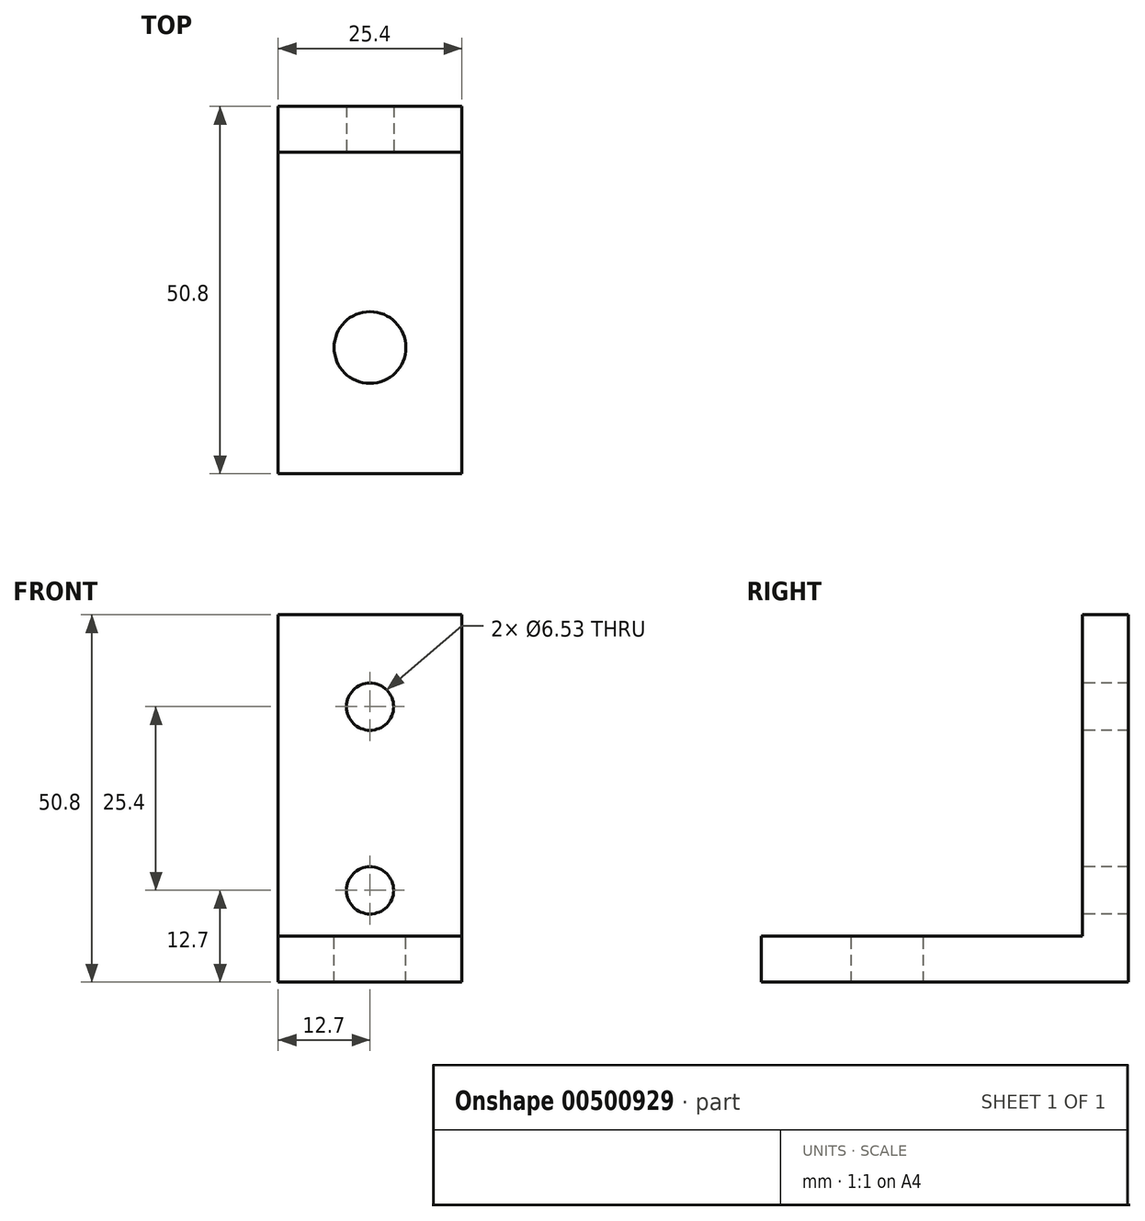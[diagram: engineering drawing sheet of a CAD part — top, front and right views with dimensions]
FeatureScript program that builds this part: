
annotation { "Feature Type Name" : "Feature", "Feature Type Description" : "" }
export const myFeature = defineFeature(function(context is Context, id is Id, definition is map)
    precondition{}
    {
        {
            var Q0;
            Q0=qCreatedBy(makeId("Right.planeOp"),FACE);
            var sketch = newSketch(context, id + "F0", { "sketchPlane" : qUnion([Q0])});
            skLineSegment(sketch, "E0.bottom", {"start": v(0, 0) * mm, "end": v(-50.8, 0) * mm});
            skLineSegment(sketch, "E0.top", {"start": v(0, 6.35) * mm, "end": v(-50.8, 6.35) * mm});
            skLineSegment(sketch, "E0.left", {"start": v(0, 0) * mm, "end": v(0, 6.35) * mm});
            skLineSegment(sketch, "E0.right", {"start": v(-50.8, 0) * mm, "end": v(-50.8, 6.35) * mm});
            skLineSegment(sketch, "E1.bottom", {"start": v(0, 0) * mm, "end": v(-6.35, 0) * mm});
            skLineSegment(sketch, "E1.top", {"start": v(0, 50.8) * mm, "end": v(-6.35, 50.8) * mm});
            skLineSegment(sketch, "E1.left", {"start": v(0, 0) * mm, "end": v(0, 50.8) * mm});
            skLineSegment(sketch, "E1.right", {"start": v(-6.35, 0) * mm, "end": v(-6.35, 50.8) * mm});
            skSolve(sketch);
        }
        {
            var Q0;
            {var subQ0=sQuery(id+"F0.wireOp",EDGE,"E0.bottom");Q0=makeQuery(id+"F0.imprint","IMPRINT",FACE,{"disambiguationData":[TD([[makeQuery(id+"F0.imprint","IMPRINT",EDGE,{"derivedFrom":subQ0}),-1.0]])]});}
            var Q1;
            {var subQ5=sQuery(id+"F0.wireOp",EDGE,"E1.bottom");Q1=makeQuery(id+"F0.imprint","IMPRINT",FACE,{"disambiguationData":[TD([[makeQuery(id+"F0.imprint","IMPRINT",EDGE,{"derivedFrom":subQ5}),-1.0]])]});}
            var Q2;
            {var subQ5=sQuery(id+"F0.wireOp",EDGE,"E1.top");Q2=makeQuery(id+"F0.imprint","IMPRINT",FACE,{"disambiguationData":[TD([[makeQuery(id+"F0.imprint","IMPRINT",EDGE,{"derivedFrom":subQ5}),1.0]])]});}
            extrude(context, id + "F1", {"entities" : qUnion([Q0, Q1, Q2]), "depth" : 25.4 * mm, "offsetDistance" : 25.4 * mm});
        }
        {
            var Q0;
            Q0=makeQuery(id+"F1.opExtrude","SWEPT_FACE",FACE,{"disambiguationData":[OSD([sQuery(id+"F0.wireOp",EDGE,"E0.top")])]});
            var sketch = newSketch(context, id + "F2", { "sketchPlane" : qUnion([Q0])});
            skCircle(sketch, "E2", {"center": v(12.7, -33.34) * mm, "radius": 4.96 * mm});
            skSolve(sketch);
        }
        {
            var Q0;
            Q0=makeQuery(id+"F2.imprint","IMPRINT",FACE,{"disambiguationData":[TD([[makeQuery(id+"F2.imprint","IMPRINT",EDGE,{"derivedFrom":sQuery(id+"F2.wireOp",EDGE,"E2")}),1.0]])]});
            extrude(context, id + "F3", {"entities" : qUnion([Q0]), "operationType" : NewBodyOperationType.REMOVE, "oppositeDirection" : true, "depth" : 25.4 * mm, "offsetDistance" : 25.4 * mm});
        }
        {
            var Q0;
            Q0=makeQuery(id+"F1.opExtrude","SWEPT_FACE",FACE,{"disambiguationData":[OSD([sQuery(id+"F0.wireOp",EDGE,"E1.right")])]});
            var sketch = newSketch(context, id + "F4", { "sketchPlane" : qUnion([Q0])});
            skSolve(sketch);
        }
        {
            var Q0;
            {var subQ0=sQuery(id+"F0.wireOp",EDGE,"E1.right");Q0=makeQuery(id+"F4.imprint","IMPRINT",FACE,{"disambiguationData":[TD([[makeQuery(id+"F4.imprint","IMPRINT",EDGE,{"derivedFrom":makeQuery(id+"F1.opExtrude","CAP_EDGE",EDGE,{"disambiguationData":[OSD([subQ0])],"isStart":true})}),-1.0]])]});}
            var sketch = newSketch(context, id + "F5", { "sketchPlane" : qUnion([Q0])});
            skCircle(sketch, "E3", {"center": v(12.7, 12.7) * mm, "radius": 3.26 * mm});
            skCircle(sketch, "E4", {"center": v(12.7, 38.1) * mm, "radius": 3.26 * mm});
            skSolve(sketch);
        }
        {
            var Q0;
            Q0 = qSketchRegion(id + "F5", true);
            extrude(context, id + "F6", {"entities" : qUnion([Q0]), "operationType" : NewBodyOperationType.REMOVE, "oppositeDirection" : true, "depth" : 25.4 * mm, "offsetDistance" : 25.4 * mm});
        }
    });
